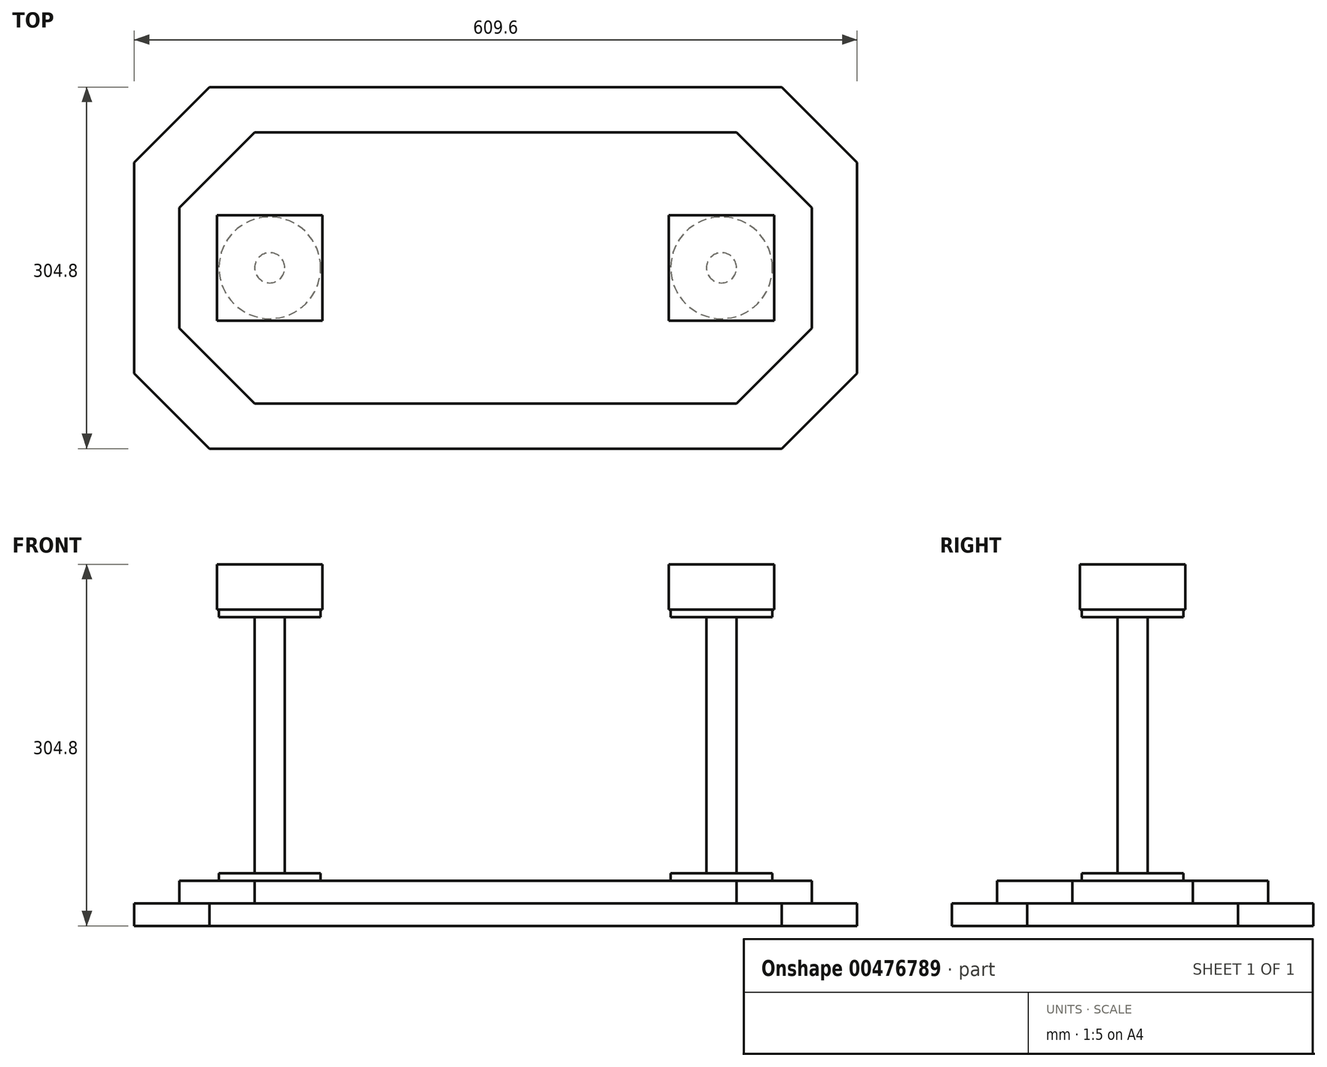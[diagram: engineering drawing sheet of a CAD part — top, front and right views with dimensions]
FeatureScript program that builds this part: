
annotation { "Feature Type Name" : "Feature", "Feature Type Description" : "" }
export const myFeature = defineFeature(function(context is Context, id is Id, definition is map)
    precondition{}
    {
        {
            var Q0;
            Q0=qCreatedBy(makeId("Top.planeOp"),FACE);
            var sketch = newSketch(context, id + "F0", { "sketchPlane" : qUnion([Q0])});
            skLineSegment(sketch, "E0.bottom", {"start": v(304.8, 152.4) * mm, "end": v(-304.8, 152.4) * mm});
            skLineSegment(sketch, "E0.top", {"start": v(304.8, -152.4) * mm, "end": v(-304.8, -152.4) * mm});
            skLineSegment(sketch, "E0.left", {"start": v(304.8, 152.4) * mm, "end": v(304.8, -152.4) * mm});
            skLineSegment(sketch, "E0.right", {"start": v(-304.8, 152.4) * mm, "end": v(-304.8, -152.4) * mm});
            skPoint(sketch, "E0.middle", {"position": v(0, 0) * mm});
            skSolve(sketch);
        }
        {
            var Q0;
            Q0=makeQuery(id+"F0.imprint","IMPRINT",FACE,{"disambiguationData":[TD([[makeQuery(id+"F0.imprint","IMPRINT",EDGE,{"derivedFrom":sQuery(id+"F0.wireOp",EDGE,"E0.bottom")}),1.0]])]});
            extrude(context, id + "F1", {"entities" : qUnion([Q0]), "depth" : 19.05 * mm});
        }
        {
            var Q0;
            Q0=makeQuery(id+"F1.opExtrude","CAP_FACE",FACE,{"disambiguationData":[OSD([sQuery(id+"F0.wireOp",EDGE,"E0.bottom"),sQuery(id+"F0.wireOp",EDGE,"E0.top"),sQuery(id+"F0.wireOp",EDGE,"E0.left"),sQuery(id+"F0.wireOp",EDGE,"E0.right")])],"isStart":false});
            var sketch = newSketch(context, id + "F2", { "sketchPlane" : qUnion([Q0])});
            skLineSegment(sketch, "E1.0", {"start": v(266.7, 114.3) * mm, "end": v(-266.7, 114.3) * mm});
            skLineSegment(sketch, "E1.1", {"start": v(266.7, 114.3) * mm, "end": v(266.7, -114.3) * mm});
            skLineSegment(sketch, "E1.2", {"start": v(266.7, -114.3) * mm, "end": v(-266.7, -114.3) * mm});
            skLineSegment(sketch, "E1.3", {"start": v(-266.7, 114.3) * mm, "end": v(-266.7, -114.3) * mm});
            skSolve(sketch);
        }
        {
            var Q0;
            Q0=makeQuery(id+"F2.imprint","IMPRINT",FACE,{"disambiguationData":[TD([[makeQuery(id+"F2.imprint","IMPRINT",EDGE,{"derivedFrom":sQuery(id+"F2.wireOp",EDGE,"E1.0")}),1.0]])]});
            extrude(context, id + "F3", {"entities" : qUnion([Q0]), "operationType" : NewBodyOperationType.ADD, "depth" : 19.05 * mm});
        }
        {
            var Q0;
            Q0=makeQuery(id+"F3.opExtrude","CAP_FACE",FACE,{"disambiguationData":[OSD([sQuery(id+"F2.wireOp",EDGE,"E1.0"),sQuery(id+"F2.wireOp",EDGE,"E1.1"),sQuery(id+"F2.wireOp",EDGE,"E1.2"),sQuery(id+"F2.wireOp",EDGE,"E1.3")])],"isStart":false});
            var sketch = newSketch(context, id + "F4", { "sketchPlane" : qUnion([Q0])});
            skCircle(sketch, "E2", {"center": v(-190.5, 0) * mm, "radius": 42.86 * mm});
            skCircle(sketch, "E3", {"center": v(190.5, 0) * mm, "radius": 42.86 * mm});
            skLineSegment(sketch, "E4", {"start": v(-190.5, 0) * mm, "end": v(190.5, 0) * mm, "construction": true});
            skPoint(sketch, "E5", {"position": v(0, 0) * mm});
            skSolve(sketch);
        }
        {
            var Q0;
            Q0 = qSketchRegion(id + "F4", true);
            extrude(context, id + "F5", {"entities" : qUnion([Q0]), "operationType" : NewBodyOperationType.ADD, "depth" : 6.35 * mm});
        }
        {
            var Q0;
            Q0=makeQuery(id+"F5.opExtrude","CAP_FACE",FACE,{"disambiguationData":[OSD([sQuery(id+"F4.wireOp",EDGE,"E2")])],"isStart":false});
            var sketch = newSketch(context, id + "F6", { "sketchPlane" : qUnion([Q0])});
            skCircle(sketch, "E6", {"center": v(-190.5, 0) * mm, "radius": 12.7 * mm});
            skCircle(sketch, "E7", {"center": v(190.5, 0) * mm, "radius": 12.7 * mm});
            skSolve(sketch);
        }
        {
            var Q0;
            Q0=makeQuery(id+"F6.imprint","IMPRINT",FACE,{"disambiguationData":[TD([[makeQuery(id+"F6.imprint","IMPRINT",EDGE,{"derivedFrom":sQuery(id+"F6.wireOp",EDGE,"E6")}),1.0]])]});
            var Q1;
            Q1=makeQuery(id+"F6.imprint","IMPRINT",FACE,{"disambiguationData":[TD([[makeQuery(id+"F6.imprint","IMPRINT",EDGE,{"derivedFrom":sQuery(id+"F6.wireOp",EDGE,"E7")}),1.0]])]});
            extrude(context, id + "F7", {"entities" : qUnion([Q0, Q1]), "operationType" : NewBodyOperationType.ADD, "depth" : 215.9 * mm});
        }
        {
            var Q0;
            Q0=makeQuery(id+"F7.opExtrude","CAP_FACE",FACE,{"disambiguationData":[OSD([sQuery(id+"F6.wireOp",EDGE,"E6")])],"isStart":false});
            var sketch = newSketch(context, id + "F8", { "sketchPlane" : qUnion([Q0])});
            skCircle(sketch, "E8", {"center": v(-190.5, 0) * mm, "radius": 42.86 * mm});
            skCircle(sketch, "E9", {"center": v(190.5, 0) * mm, "radius": 42.86 * mm});
            skSolve(sketch);
        }
        {
            var Q0;
            Q0 = qSketchRegion(id + "F8", true);
            extrude(context, id + "F9", {"entities" : qUnion([Q0]), "operationType" : NewBodyOperationType.ADD, "depth" : 6.35 * mm});
        }
        {
            var Q0;
            Q0=makeQuery(id+"F9.opExtrude","CAP_FACE",FACE,{"disambiguationData":[OSD([sQuery(id+"F8.wireOp",EDGE,"E8")])],"isStart":false});
            var sketch = newSketch(context, id + "F10", { "sketchPlane" : qUnion([Q0])});
            skLineSegment(sketch, "E10.bottom", {"start": v(-146.05, 44.45) * mm, "end": v(-234.95, 44.45) * mm});
            skLineSegment(sketch, "E10.top", {"start": v(-146.05, -44.45) * mm, "end": v(-234.95, -44.45) * mm});
            skLineSegment(sketch, "E10.left", {"start": v(-146.05, 44.45) * mm, "end": v(-146.05, -44.45) * mm});
            skLineSegment(sketch, "E10.right", {"start": v(-234.95, 44.45) * mm, "end": v(-234.95, -44.45) * mm});
            skPoint(sketch, "E10.middle", {"position": v(-190.5, 0) * mm});
            skLineSegment(sketch, "E11.bottom", {"start": v(234.95, 44.45) * mm, "end": v(146.05, 44.45) * mm});
            skLineSegment(sketch, "E11.top", {"start": v(234.95, -44.45) * mm, "end": v(146.05, -44.45) * mm});
            skLineSegment(sketch, "E11.left", {"start": v(234.95, 44.45) * mm, "end": v(234.95, -44.45) * mm});
            skLineSegment(sketch, "E11.right", {"start": v(146.05, 44.45) * mm, "end": v(146.05, -44.45) * mm});
            skPoint(sketch, "E11.middle", {"position": v(190.5, 0) * mm});
            skSolve(sketch);
        }
        {
            var Q0;
            Q0 = qSketchRegion(id + "F10", true);
            extrude(context, id + "F11", {"entities" : qUnion([Q0]), "operationType" : NewBodyOperationType.ADD, "depth" : 38.1 * mm});
        }
        {
            var Q0;
            Q0=makeQuery(id+"F3.opExtrude","SWEPT_EDGE",EDGE,{"disambiguationData":[OSD([sQuery(id+"F2.wireOp",EDGE,"E1.0"),sQuery(id+"F2.wireOp",EDGE,"E1.3")])]});
            var Q1;
            Q1=makeQuery(id+"F3.opExtrude","SWEPT_EDGE",EDGE,{"disambiguationData":[OSD([sQuery(id+"F2.wireOp",EDGE,"E1.2"),sQuery(id+"F2.wireOp",EDGE,"E1.3")])]});
            var Q2;
            Q2=makeQuery(id+"F1.opExtrude","SWEPT_EDGE",EDGE,{"disambiguationData":[OSD([sQuery(id+"F0.wireOp",EDGE,"E0.top"),sQuery(id+"F0.wireOp",EDGE,"E0.right")])]});
            var Q3;
            Q3=makeQuery(id+"F1.opExtrude","SWEPT_EDGE",EDGE,{"disambiguationData":[OSD([sQuery(id+"F0.wireOp",EDGE,"E0.bottom"),sQuery(id+"F0.wireOp",EDGE,"E0.right")])]});
            var Q4;
            Q4=makeQuery(id+"F3.opExtrude","SWEPT_EDGE",EDGE,{"disambiguationData":[OSD([sQuery(id+"F2.wireOp",EDGE,"E1.0"),sQuery(id+"F2.wireOp",EDGE,"E1.1")])]});
            var Q5;
            Q5=makeQuery(id+"F3.opExtrude","SWEPT_EDGE",EDGE,{"disambiguationData":[OSD([sQuery(id+"F2.wireOp",EDGE,"E1.1"),sQuery(id+"F2.wireOp",EDGE,"E1.2")])]});
            var Q6;
            Q6=makeQuery(id+"F1.opExtrude","SWEPT_EDGE",EDGE,{"disambiguationData":[OSD([sQuery(id+"F0.wireOp",EDGE,"E0.bottom"),sQuery(id+"F0.wireOp",EDGE,"E0.left")])]});
            var Q7;
            Q7=makeQuery(id+"F1.opExtrude","SWEPT_EDGE",EDGE,{"disambiguationData":[OSD([sQuery(id+"F0.wireOp",EDGE,"E0.top"),sQuery(id+"F0.wireOp",EDGE,"E0.left")])]});
            chamfer(context, id + "F12", {"entities" : qUnion([Q0, Q1, Q2, Q3, Q4, Q5, Q6, Q7]), "width" : 63.5 * mm, "tangentPropagation" : true});
        }
    });
